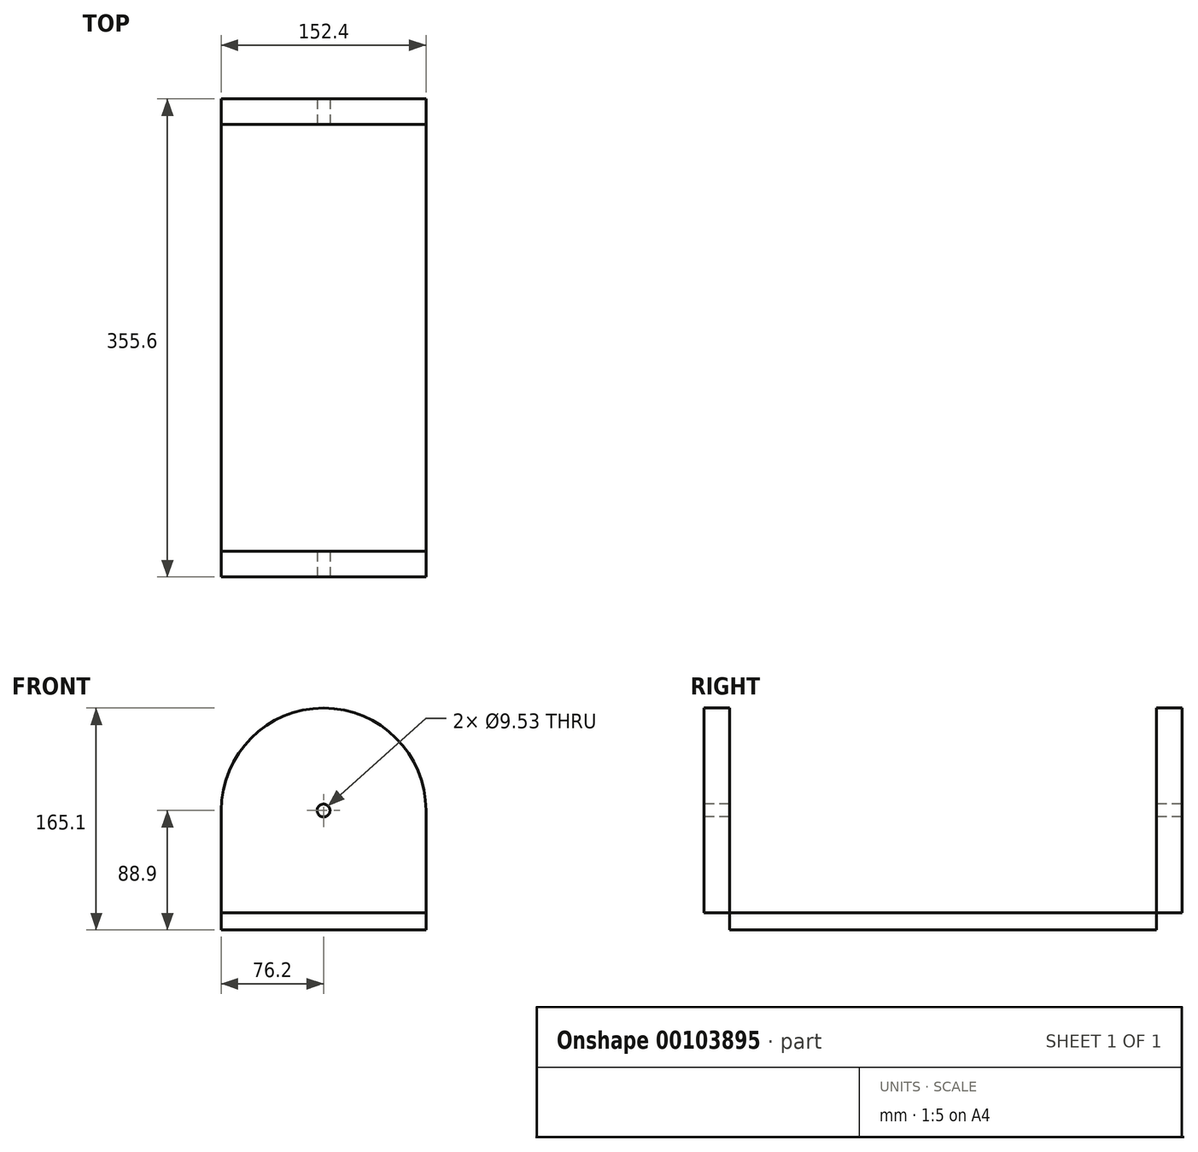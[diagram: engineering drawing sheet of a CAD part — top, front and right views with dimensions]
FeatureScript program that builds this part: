
annotation { "Feature Type Name" : "Feature", "Feature Type Description" : "" }
export const myFeature = defineFeature(function(context is Context, id is Id, definition is map)
    precondition{}
    {
        {
            var Q0;
            Q0=qCreatedBy(makeId("Right.planeOp"),FACE);
            var sketch = newSketch(context, id + "F0", { "sketchPlane" : qUnion([Q0])});
            skLineSegment(sketch, "E0.bottom", {"start": v(0, 0) * mm, "end": v(19.05, 0) * mm});
            skLineSegment(sketch, "E0.top", {"start": v(0, 165.1) * mm, "end": v(19.05, 165.1) * mm});
            skLineSegment(sketch, "E0.left", {"start": v(0, 0) * mm, "end": v(0, 165.1) * mm});
            skLineSegment(sketch, "E0.right", {"start": v(19.05, 0) * mm, "end": v(19.05, 165.1) * mm});
            skLineSegment(sketch, "E1.bottom", {"start": v(0, 0) * mm, "end": v(355.6, 0) * mm});
            skLineSegment(sketch, "E1.top", {"start": v(0, 12.7) * mm, "end": v(355.6, 12.7) * mm});
            skLineSegment(sketch, "E1.left", {"start": v(0, 0) * mm, "end": v(0, 12.7) * mm});
            skLineSegment(sketch, "E1.right", {"start": v(355.6, 0) * mm, "end": v(355.6, 12.7) * mm});
            skLineSegment(sketch, "E2.bottom", {"start": v(355.6, 0) * mm, "end": v(336.55, 0) * mm});
            skLineSegment(sketch, "E2.top", {"start": v(355.6, 165.1) * mm, "end": v(336.55, 165.1) * mm});
            skLineSegment(sketch, "E2.left", {"start": v(355.6, 0) * mm, "end": v(355.6, 165.1) * mm});
            skLineSegment(sketch, "E2.right", {"start": v(336.55, 0) * mm, "end": v(336.55, 165.1) * mm});
            skSolve(sketch);
        }
        {
            var Q0;
            {var subQ0=sQuery(id+"F0.wireOp",EDGE,"E0.top");Q0=makeQuery(id+"F0.imprint","IMPRINT",FACE,{"disambiguationData":[TD([[makeQuery(id+"F0.imprint","IMPRINT",EDGE,{"derivedFrom":subQ0}),-1.0]])]});}
            var Q1;
            {var subQ5=sQuery(id+"F0.wireOp",EDGE,"E1.left");Q1=makeQuery(id+"F0.imprint","IMPRINT",FACE,{"disambiguationData":[TD([[makeQuery(id+"F0.imprint","IMPRINT",EDGE,{"derivedFrom":subQ5}),-1.0]])]});}
            var Q2;
            {var subQ0=sQuery(id+"F0.wireOp",EDGE,"E1.bottom");var subQ1=sQuery(id+"F0.wireOp",EDGE,"E0.right");var subQ2=makeQuery(id+"F0.imprint","INTERSECT",VERTEX,{"derivedFrom":[subQ1,subQ0]});Q2=makeQuery(id+"F0.imprint","IMPRINT",FACE,{"disambiguationData":[TD([[makeQuery(id+"F0.imprint","IMPRINT",EDGE,{"disambiguationData":[TD([[subQ2,-1.0]])],"derivedFrom":subQ1}),-1.0]])]});}
            var Q3;
            {var subQ5=sQuery(id+"F0.wireOp",EDGE,"E2.top");Q3=makeQuery(id+"F0.imprint","IMPRINT",FACE,{"disambiguationData":[TD([[makeQuery(id+"F0.imprint","IMPRINT",EDGE,{"derivedFrom":subQ5}),1.0]])]});}
            var Q4;
            {var subQ5=sQuery(id+"F0.wireOp",EDGE,"E2.bottom");Q4=makeQuery(id+"F0.imprint","IMPRINT",FACE,{"disambiguationData":[TD([[makeQuery(id+"F0.imprint","IMPRINT",EDGE,{"derivedFrom":subQ5}),-1.0]])]});}
            extrude(context, id + "F1", {"entities" : qUnion([Q0, Q1, Q2, Q3, Q4]), "depth" : 152.4 * mm});
        }
        {
            var Q0;
            Q0=qCreatedBy(makeId("Front.planeOp"),FACE);
            var sketch = newSketch(context, id + "F2", { "sketchPlane" : qUnion([Q0])});
            skCircle(sketch, "E3", {"center": v(76.2, 88.9) * mm, "radius": 4.76 * mm});
            skSolve(sketch);
        }
        {
            var Q0;
            Q0=makeQuery(id+"F2.imprint","IMPRINT",FACE,{"disambiguationData":[TD([[makeQuery(id+"F2.imprint","IMPRINT",EDGE,{"derivedFrom":sQuery(id+"F2.wireOp",EDGE,"E3")}),1.0]])]});
            extrude(context, id + "F3", {"entities" : qUnion([Q0]), "operationType" : NewBodyOperationType.REMOVE, "oppositeDirection" : true, "depth" : 406.4 * mm});
        }
        {
            var Q0;
            Q0=makeQuery(id+"F1.opExtrude","CAP_EDGE",EDGE,{"disambiguationData":[OSD([sQuery(id+"F0.wireOp",EDGE,"E2.top")])],"isStart":false});
            var Q1;
            Q1=makeQuery(id+"F1.opExtrude","CAP_EDGE",EDGE,{"disambiguationData":[OSD([sQuery(id+"F0.wireOp",EDGE,"E0.top")])],"isStart":false});
            var Q2;
            Q2=makeQuery(id+"F1.opExtrude","CAP_EDGE",EDGE,{"disambiguationData":[OSD([sQuery(id+"F0.wireOp",EDGE,"E0.top")])],"isStart":true});
            var Q3;
            Q3=makeQuery(id+"F1.opExtrude","CAP_EDGE",EDGE,{"disambiguationData":[OSD([sQuery(id+"F0.wireOp",EDGE,"E2.top")])],"isStart":true});
            fillet(context, id + "F4", {"entities" : qUnion([Q0, Q1, Q2, Q3]), "radius" : 76.2 * mm, "tangentPropagation" : true, "allowEdgeOverflow" : false});
        }
    });
